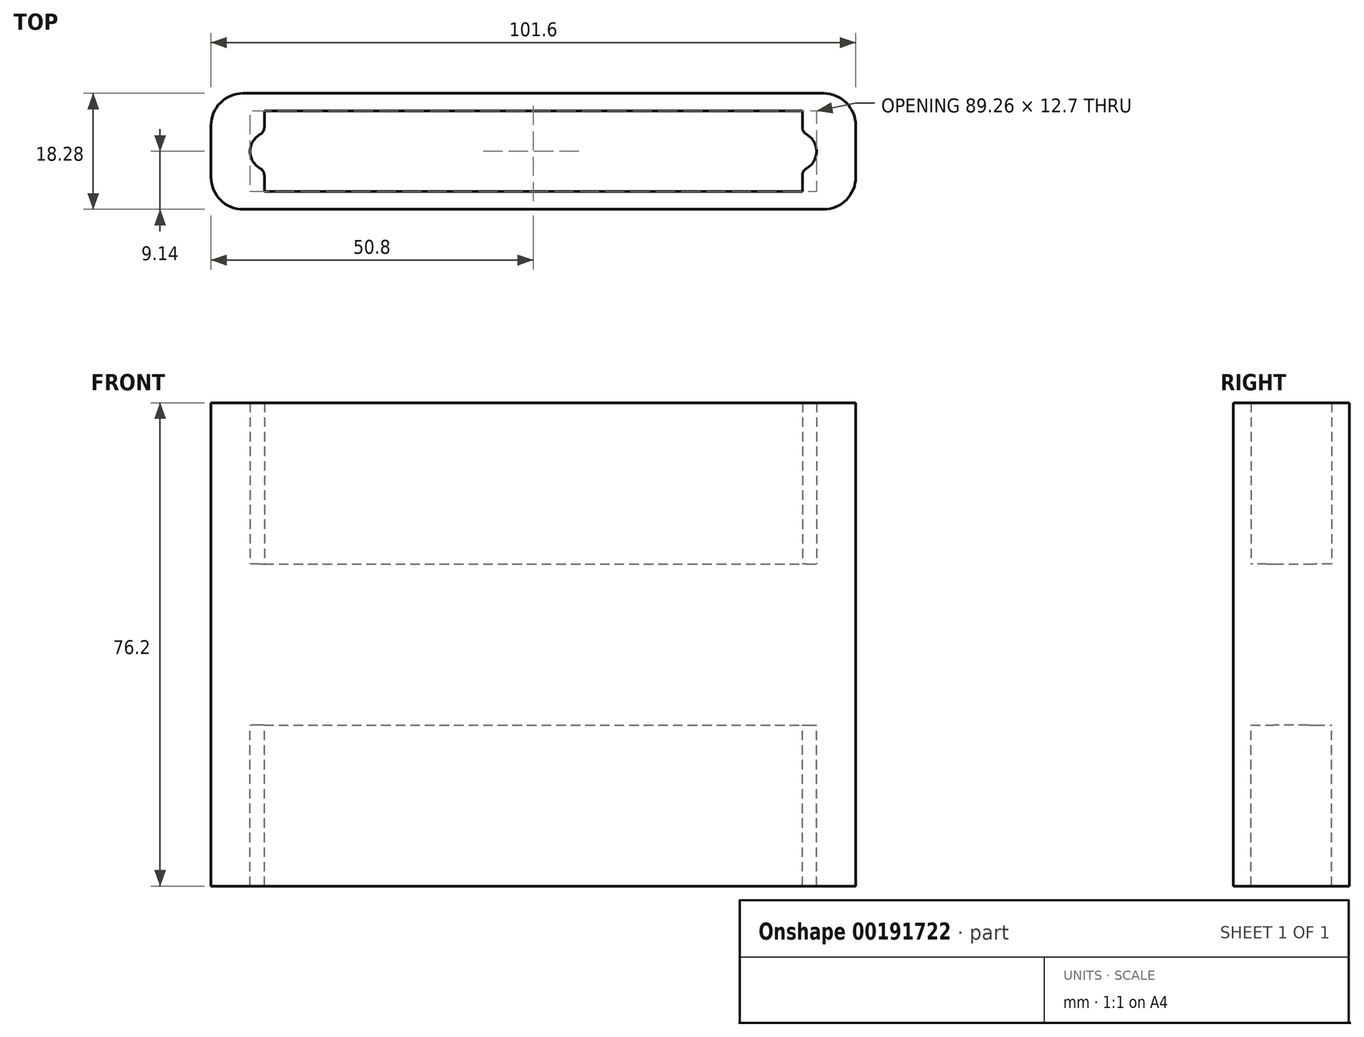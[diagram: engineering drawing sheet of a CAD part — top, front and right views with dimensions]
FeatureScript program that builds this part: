
annotation { "Feature Type Name" : "Feature", "Feature Type Description" : "" }
export const myFeature = defineFeature(function(context is Context, id is Id, definition is map)
    precondition{}
    {
        {
            var Q0;
            Q0=qCreatedBy(makeId("Top.planeOp"),FACE);
            var sketch = newSketch(context, id + "F0", { "sketchPlane" : qUnion([Q0])});
            skLineSegment(sketch, "E0.bottom", {"start": v(-50.8, 9.14) * mm, "end": v(50.8, 9.14) * mm});
            skLineSegment(sketch, "E0.top", {"start": v(-50.8, -9.14) * mm, "end": v(50.8, -9.14) * mm});
            skLineSegment(sketch, "E0.left", {"start": v(-50.8, 9.14) * mm, "end": v(-50.8, -9.14) * mm});
            skLineSegment(sketch, "E0.right", {"start": v(50.8, 9.14) * mm, "end": v(50.8, -9.14) * mm});
            skSolve(sketch);
        }
        {
            var Q0;
            Q0 = qSketchRegion(id + "F0", true);
            extrude(context, id + "F1", {"entities" : qUnion([Q0]), "endBound" : BoundingType.SYMMETRIC, "depth" : 25.4 * mm});
        }
        {
            var Q0;
            Q0=makeQuery(id+"F1.opExtrude","CAP_FACE",FACE,{"disambiguationData":[OSD([sQuery(id+"F0.wireOp",EDGE,"E0.bottom"),sQuery(id+"F0.wireOp",EDGE,"E0.top"),sQuery(id+"F0.wireOp",EDGE,"E0.left"),sQuery(id+"F0.wireOp",EDGE,"E0.right")])],"isStart":false});
            var sketch = newSketch(context, id + "F2", { "sketchPlane" : qUnion([Q0])});
            skPoint(sketch, "E1", {"position": v(-41.55, 0) * mm});
            skPoint(sketch, "E2", {"position": v(41.55, 0) * mm});
            skLineSegment(sketch, "E3.bottom", {"start": v(-42.4, 6.35) * mm, "end": v(42.4, 6.35) * mm});
            skLineSegment(sketch, "E3.top", {"start": v(-42.4, -6.35) * mm, "end": v(42.4, -6.35) * mm});
            skLineSegment(sketch, "E3.left", {"start": v(-42.4, 6.35) * mm, "end": v(-42.4, 2.96) * mm});
            skLineSegment(sketch, "E3.right", {"start": v(42.4, 6.35) * mm, "end": v(42.4, 2.96) * mm});
            skArc(sketch, "E4", {"start": v(-42.4, 2.96) * mm, "mid": v(-44.63, 0) * mm, "end": v(-42.4, -2.96) * mm});
            skArc(sketch, "E5", {"start": v(42.4, -2.96) * mm, "mid": v(44.63, 0) * mm, "end": v(42.4, 2.96) * mm});
            skLineSegment(sketch, "E6.trimOffspring", {"start": v(-42.4, -2.96) * mm, "end": v(-42.4, -6.35) * mm});
            skLineSegment(sketch, "E7.trimOffspring", {"start": v(42.4, -2.96) * mm, "end": v(42.4, -6.35) * mm});
            skSolve(sketch);
        }
        {
            var Q0;
            Q0=makeQuery(id+"F1.opExtrude","CAP_FACE",FACE,{"disambiguationData":[OSD([sQuery(id+"F0.wireOp",EDGE,"E0.bottom"),sQuery(id+"F0.wireOp",EDGE,"E0.top"),sQuery(id+"F0.wireOp",EDGE,"E0.left"),sQuery(id+"F0.wireOp",EDGE,"E0.right")])],"isStart":true});
            var sketch = newSketch(context, id + "F3", { "sketchPlane" : qUnion([Q0])});
            skPoint(sketch, "E8", {"position": v(-41.55, 0) * mm});
            skPoint(sketch, "E9", {"position": v(41.55, 0) * mm});
            skLineSegment(sketch, "E10.bottom", {"start": v(-42.4, 6.35) * mm, "end": v(42.4, 6.35) * mm});
            skLineSegment(sketch, "E10.top", {"start": v(-42.4, -6.35) * mm, "end": v(42.4, -6.35) * mm});
            skLineSegment(sketch, "E10.left", {"start": v(-42.4, 6.35) * mm, "end": v(-42.4, 2.96) * mm});
            skLineSegment(sketch, "E10.right", {"start": v(42.4, 6.35) * mm, "end": v(42.4, 2.96) * mm});
            skArc(sketch, "E11", {"start": v(-42.4, 2.96) * mm, "mid": v(-44.63, 0) * mm, "end": v(-42.4, -2.96) * mm});
            skArc(sketch, "E12", {"start": v(42.4, -2.96) * mm, "mid": v(44.63, 0) * mm, "end": v(42.4, 2.96) * mm});
            skLineSegment(sketch, "E13.trimOffspring", {"start": v(-42.4, -2.96) * mm, "end": v(-42.4, -6.35) * mm});
            skLineSegment(sketch, "E14.trimOffspring", {"start": v(42.4, -2.96) * mm, "end": v(42.4, -6.35) * mm});
            skSolve(sketch);
        }
        {
            var Q0;
            Q0=makeQuery(id+"F2.imprint","IMPRINT",FACE,{"disambiguationData":[TD([[makeQuery(id+"F2.imprint","IMPRINT",EDGE,{"derivedFrom":sQuery(id+"F2.wireOp",EDGE,"E3.bottom")}),1.0]])]});
            extrude(context, id + "F4", {"entities" : qUnion([Q0]), "operationType" : NewBodyOperationType.ADD, "depth" : 25.4 * mm});
        }
        {
            var Q0;
            Q0=makeQuery(id+"F3.imprint","IMPRINT",FACE,{"disambiguationData":[TD([[makeQuery(id+"F3.imprint","IMPRINT",EDGE,{"derivedFrom":sQuery(id+"F3.wireOp",EDGE,"E10.bottom")}),1.0]])]});
            extrude(context, id + "F5", {"entities" : qUnion([Q0]), "operationType" : NewBodyOperationType.ADD, "depth" : 25.4 * mm});
        }
        {
            var Q0;
            Q0=makeQuery(id+"F4.opExtrude","SWEPT_EDGE",EDGE,{"disambiguationData":[OSD([sQuery(id+"F2.wireOp",EDGE,"E3.left"),sQuery(id+"F2.wireOp",EDGE,"E4")])]});
            var Q1;
            Q1=makeQuery(id+"F4.opExtrude","SWEPT_EDGE",EDGE,{"disambiguationData":[OSD([sQuery(id+"F2.wireOp",EDGE,"E4"),sQuery(id+"F2.wireOp",EDGE,"E6.trimOffspring")])]});
            var Q2;
            Q2=makeQuery(id+"F4.opExtrude","SWEPT_EDGE",EDGE,{"disambiguationData":[OSD([sQuery(id+"F2.wireOp",EDGE,"E3.right"),sQuery(id+"F2.wireOp",EDGE,"E5")])]});
            var Q3;
            Q3=makeQuery(id+"F4.opExtrude","SWEPT_EDGE",EDGE,{"disambiguationData":[OSD([sQuery(id+"F2.wireOp",EDGE,"E5"),sQuery(id+"F2.wireOp",EDGE,"E7.trimOffspring")])]});
            var Q4;
            Q4=makeQuery(id+"F5.opExtrude","SWEPT_EDGE",EDGE,{"disambiguationData":[OSD([sQuery(id+"F3.wireOp",EDGE,"E12"),sQuery(id+"F3.wireOp",EDGE,"E14.trimOffspring")])]});
            var Q5;
            Q5=makeQuery(id+"F5.opExtrude","SWEPT_EDGE",EDGE,{"disambiguationData":[OSD([sQuery(id+"F3.wireOp",EDGE,"E10.right"),sQuery(id+"F3.wireOp",EDGE,"E12")])]});
            var Q6;
            Q6=makeQuery(id+"F5.opExtrude","SWEPT_EDGE",EDGE,{"disambiguationData":[OSD([sQuery(id+"F3.wireOp",EDGE,"E11"),sQuery(id+"F3.wireOp",EDGE,"E13.trimOffspring")])]});
            var Q7;
            Q7=makeQuery(id+"F5.opExtrude","SWEPT_EDGE",EDGE,{"disambiguationData":[OSD([sQuery(id+"F3.wireOp",EDGE,"E10.left"),sQuery(id+"F3.wireOp",EDGE,"E11")])]});
            fillet(context, id + "F6", {"entities" : qUnion([Q0, Q1, Q2, Q3, Q4, Q5, Q6, Q7]), "radius" : 1.27 * mm, "tangentPropagation" : true, "allowEdgeOverflow" : false});
        }
        {
            var Q0;
            {var subQ0=sQuery(id+"F0.wireOp",EDGE,"E0.right");var subQ1=sQuery(id+"F0.wireOp",EDGE,"E0.top");Q0=makeQuery(id+"F5.boolean.opBoolean","MERGE",EDGE,{"derivedFrom":[makeQuery(id+"F4.boolean.opBoolean","MERGE",EDGE,{"derivedFrom":[makeQuery(id+"F1.opExtrude","SWEPT_EDGE",EDGE,{"disambiguationData":[OSD([subQ1,subQ0])]}),makeQuery(id+"F4.opExtrude","SWEPT_EDGE",EDGE,{"disambiguationData":[OSD([subQ1,subQ0])]})]}),makeQuery(id+"F5.opExtrude","SWEPT_EDGE",EDGE,{"disambiguationData":[OSD([subQ1,subQ0])]})]});}
            var Q1;
            {var subQ0=sQuery(id+"F0.wireOp",EDGE,"E0.right");var subQ1=sQuery(id+"F0.wireOp",EDGE,"E0.bottom");Q1=makeQuery(id+"F5.boolean.opBoolean","MERGE",EDGE,{"derivedFrom":[makeQuery(id+"F4.boolean.opBoolean","MERGE",EDGE,{"derivedFrom":[makeQuery(id+"F1.opExtrude","SWEPT_EDGE",EDGE,{"disambiguationData":[OSD([subQ1,subQ0])]}),makeQuery(id+"F4.opExtrude","SWEPT_EDGE",EDGE,{"disambiguationData":[OSD([subQ1,subQ0])]})]}),makeQuery(id+"F5.opExtrude","SWEPT_EDGE",EDGE,{"disambiguationData":[OSD([subQ1,subQ0])]})]});}
            var Q2;
            {var subQ0=sQuery(id+"F0.wireOp",EDGE,"E0.left");var subQ1=sQuery(id+"F0.wireOp",EDGE,"E0.top");Q2=makeQuery(id+"F5.boolean.opBoolean","MERGE",EDGE,{"derivedFrom":[makeQuery(id+"F4.boolean.opBoolean","MERGE",EDGE,{"derivedFrom":[makeQuery(id+"F1.opExtrude","SWEPT_EDGE",EDGE,{"disambiguationData":[OSD([subQ1,subQ0])]}),makeQuery(id+"F4.opExtrude","SWEPT_EDGE",EDGE,{"disambiguationData":[OSD([subQ1,subQ0])]})]}),makeQuery(id+"F5.opExtrude","SWEPT_EDGE",EDGE,{"disambiguationData":[OSD([subQ1,subQ0])]})]});}
            var Q3;
            {var subQ0=sQuery(id+"F0.wireOp",EDGE,"E0.left");var subQ1=sQuery(id+"F0.wireOp",EDGE,"E0.bottom");Q3=makeQuery(id+"F5.boolean.opBoolean","MERGE",EDGE,{"derivedFrom":[makeQuery(id+"F4.boolean.opBoolean","MERGE",EDGE,{"derivedFrom":[makeQuery(id+"F1.opExtrude","SWEPT_EDGE",EDGE,{"disambiguationData":[OSD([subQ1,subQ0])]}),makeQuery(id+"F4.opExtrude","SWEPT_EDGE",EDGE,{"disambiguationData":[OSD([subQ1,subQ0])]})]}),makeQuery(id+"F5.opExtrude","SWEPT_EDGE",EDGE,{"disambiguationData":[OSD([subQ1,subQ0])]})]});}
            fillet(context, id + "F7", {"entities" : qUnion([Q0, Q1, Q2, Q3]), "radius" : 5.08 * mm, "tangentPropagation" : true, "allowEdgeOverflow" : false});
        }
    });
